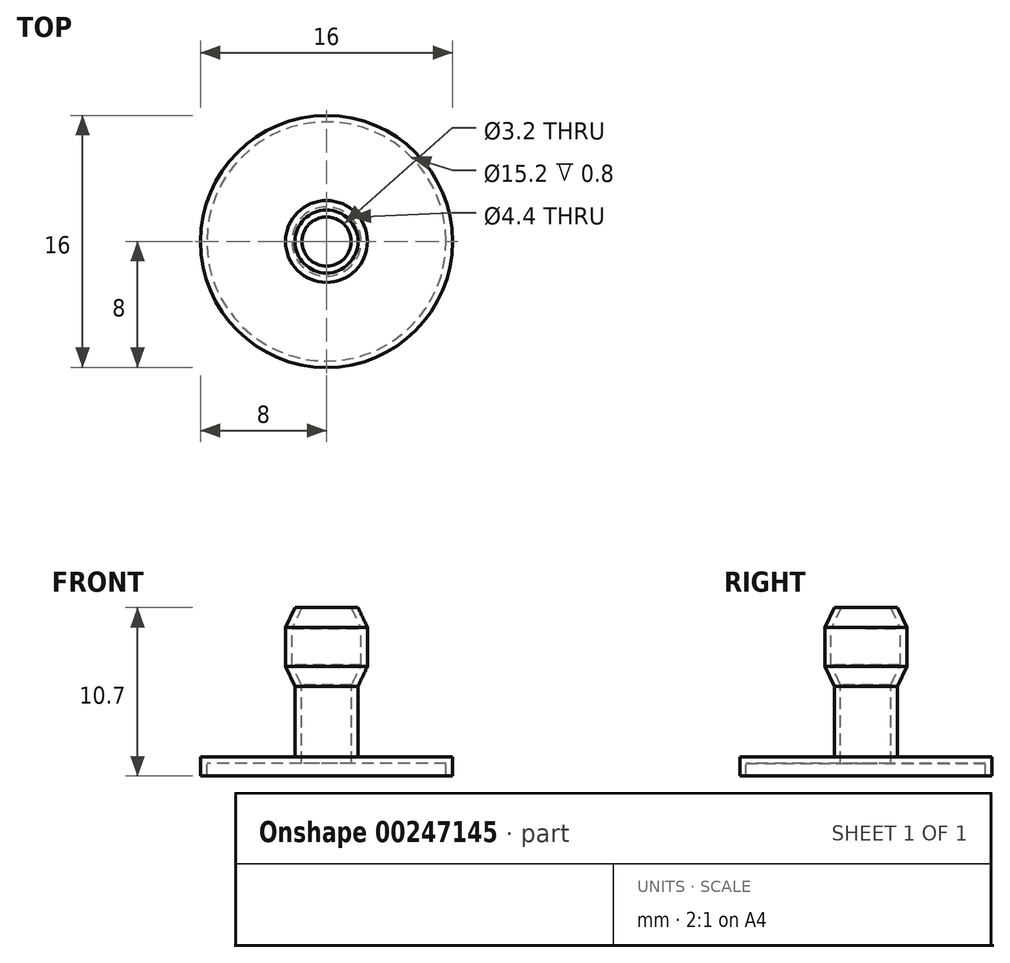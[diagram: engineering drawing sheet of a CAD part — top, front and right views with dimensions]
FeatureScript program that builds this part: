
annotation { "Feature Type Name" : "Feature", "Feature Type Description" : "" }
export const myFeature = defineFeature(function(context is Context, id is Id, definition is map)
    precondition{}
    {
        {
            var Q0;
            Q0=qCreatedBy(makeId("Right.planeOp"),FACE);
            var sketch = newSketch(context, id + "F0", { "sketchPlane" : qUnion([Q0])});
            skLineSegment(sketch, "E0.left", {"start": v(-2, 1.2) * mm, "end": v(-2, 5.7) * mm});
            skLineSegment(sketch, "E1", {"start": v(-2, 5.7) * mm, "end": v(-2.6, 6.95) * mm});
            skLineSegment(sketch, "E2", {"start": v(-2.6, 6.95) * mm, "end": v(-2.6, 9.45) * mm});
            skLineSegment(sketch, "E3", {"start": v(-2.6, 9.45) * mm, "end": v(-2, 10.7) * mm});
            skLineSegment(sketch, "E4", {"start": v(-2, 10.7) * mm, "end": v(0, 10.7) * mm});
            skLineSegment(sketch, "E5", {"start": v(-2, 10.7) * mm, "end": v(-2, 5.7) * mm, "construction": true});
            skLineSegment(sketch, "E6.bottom", {"start": v(0, 0) * mm, "end": v(-8, 0) * mm});
            skLineSegment(sketch, "E6.top", {"start": v(0, 1.2) * mm, "end": v(-8, 1.2) * mm});
            skLineSegment(sketch, "E6.left", {"start": v(0, 0) * mm, "end": v(0, 1.2) * mm});
            skLineSegment(sketch, "E6.right", {"start": v(-8, 0) * mm, "end": v(-8, 1.2) * mm});
            skLineSegment(sketch, "E7", {"start": v(0, 10.7) * mm, "end": v(0, 1.2) * mm});
            skSolve(sketch);
        }
        {
            var Q0;
            Q0 = qSketchRegion(id + "F0", true);
            var Q1;
            Q1=sQuery(id+"F0.wireOp",EDGE,"E7");
            revolve(context, id + "F1", {"entities" : qUnion([Q0]), "axis" : qUnion([Q1]), "revolveType" : RevolveType.FULL});
        }
        {
            var Q0;
            Q0=makeQuery(id+"F1.opRevolve","SWEPT_FACE",FACE,{"disambiguationData":[OSD([sQuery(id+"F0.wireOp",EDGE,"E4")])]});
            shell(context, id + "F2", {"entities" : qUnion([Q0]), "thickness" : .4 * mm});
        }
        {
            var Q0;
            Q0=makeQuery(id+"F2.opShell","OFFSET_FACE",FACE,{"disambiguationData":[OSD([sQuery(id+"F0.wireOp",EDGE,"E6.bottom")])]});
            extrude(context, id + "F3", {"entities" : qUnion([Q0]), "operationType" : NewBodyOperationType.REMOVE, "endBound" : BoundingType.UP_TO_NEXT, "oppositeDirection" : true, "depth" : 25 * mm});
        }
    });
